# Revit family: DAL_A3-Lift-Side-Door
name_source: partatom
category: Specialty Equipment
revit_build: Autodesk Revit 2016 (Build: 20150220_1215(x64)
units: mm (PartAtom-declared; Revit-internal decimal feet)

## family parameters
Always vertical = Yes
Cut with Voids When Loaded = No
Host = Wall
Part Type = Undefined
Room Calculation Point = No
Round Connector Dimension = Use Diameter
Shared = No

## types (3) — shared parameters
Car Offset = 100 mm  [stored 0.328084 ft]
Description = Dimensions indicative only! Check with your elevator consultant.
Door Height = 2100 mm
Lift Architrave Finish = Lift Architraves
Lift Doors Finish = Lift Doors
Shaft-Car Gap = 250 mm
zero-valued in all types: Door Offset

## per-type parameters (varying)
| type | Car Depth | Car Width | Door Width | Shaft Depth | Shaft Width |
| 4 Person 320kg load | 1100 mm  [stored 3.60892 ft] | 800 mm  [stored 2.62467 ft] | 700 mm | 1450 mm | 1550 mm |
| 6 Person 450kg load | 1250 mm | 1000 mm  [stored 3.28084 ft] | 800 mm  [stored 2.62467 ft] | 1650 mm | 1700 mm |
| 13 Persons 1000kg load | 2100 mm | 1100 mm  [stored 3.60892 ft] | 900 mm | 2450 mm  [stored 8.03806 ft] | 1800 mm  [stored 5.90551 ft] |

note: [stored X ft] marks values corroborated as IEEE doubles in the binary element streams (Revit-internal decimal feet)

## geometry (parser evidence)
native form markers: Sweep x3
no freeform markers — native parametric forms only
